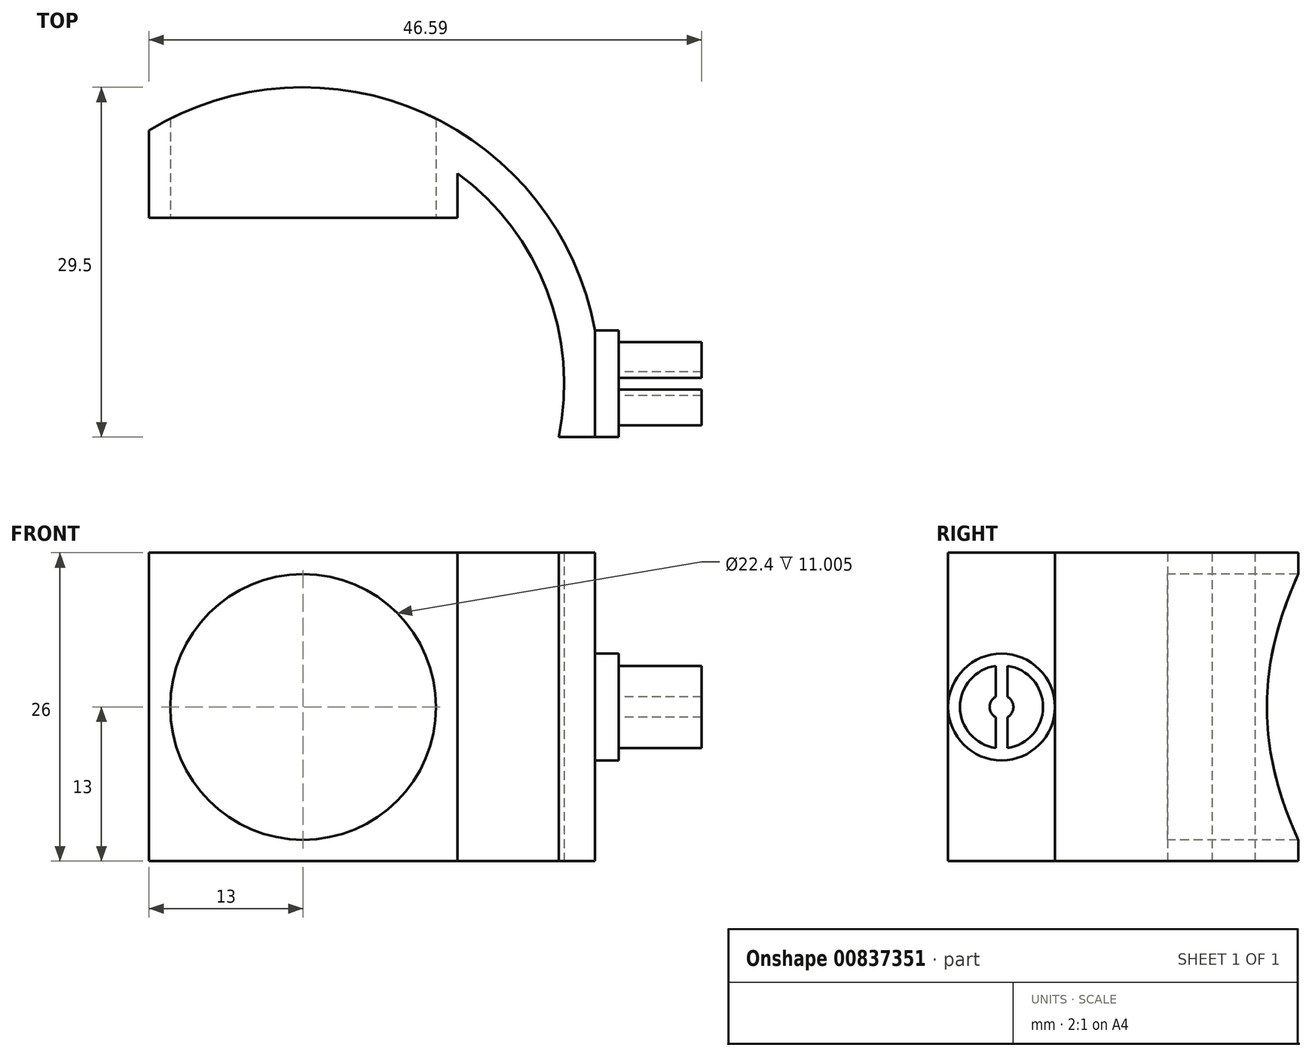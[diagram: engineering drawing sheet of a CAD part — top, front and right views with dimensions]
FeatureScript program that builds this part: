
annotation { "Feature Type Name" : "Feature", "Feature Type Description" : "" }
export const myFeature = defineFeature(function(context is Context, id is Id, definition is map)
    precondition{}
    {
        {
            var Q0;
            Q0=qCreatedBy(makeId("Top.planeOp"),FACE);
            var sketch = newSketch(context, id + "F0", { "sketchPlane" : qUnion([Q0])});
            skArc(sketch, "E0", {"start": v(21.53, -4.5) * mm, "mid": v(20.54, 7.88) * mm, "end": v(13, 17.75) * mm});
            skArc(sketch, "E1", {"start": v(24.6, 4.5) * mm, "mid": v(10.23, 22.81) * mm, "end": v(-13, 21.35) * mm});
            skLineSegment(sketch, "E2.bottom", {"start": v(13, 14) * mm, "end": v(-13, 14) * mm});
            skLineSegment(sketch, "E2.left", {"start": v(13, 14) * mm, "end": v(13, 17.75) * mm});
            skLineSegment(sketch, "E2.right", {"start": v(-13, 14) * mm, "end": v(-13, 21.35) * mm});
            skPoint(sketch, "E2.middle", {"position": v(0, 22) * mm});
            skPoint(sketch, "E2.top.end.orphan", {"position": v(-13, 30) * mm});
            skPoint(sketch, "E3.orphan", {"position": v(13, 30) * mm});
            skLineSegment(sketch, "E4", {"start": v(24.6, 4.5) * mm, "end": v(24.6, -4.5) * mm});
            skLineSegment(sketch, "E5", {"start": v(0, 0) * mm, "end": v(24.6, 0) * mm, "construction": true});
            skLineSegment(sketch, "E6", {"start": v(24.6, -4.5) * mm, "end": v(21.53, -4.5) * mm});
            skSolve(sketch);
        }
        {
            var Q0;
            Q0=makeQuery(id+"F0.imprint","IMPRINT",FACE,{"disambiguationData":[TD([[makeQuery(id+"F0.imprint","IMPRINT",EDGE,{"derivedFrom":sQuery(id+"F0.wireOp",EDGE,"E0")}),-1.0]])]});
            extrude(context, id + "F1", {"entities" : qUnion([Q0]), "depth" : 26 * mm, "offsetDistance" : 25 * mm});
        }
        {
            var Q0;
            Q0=makeQuery(id+"F1.opExtrude","SWEPT_FACE",FACE,{"disambiguationData":[OSD([sQuery(id+"F0.wireOp",EDGE,"E2.bottom")])]});
            var sketch = newSketch(context, id + "F2", { "sketchPlane" : qUnion([Q0])});
            skLineSegment(sketch, "E7", {"start": v(-13, 26) * mm, "end": v(13, 0) * mm, "construction": true});
            skLineSegment(sketch, "E8", {"start": v(-13, 0) * mm, "end": v(13, 26) * mm, "construction": true});
            skCircle(sketch, "E9", {"center": v(0, 13) * mm, "radius": 11.2 * mm});
            skSolve(sketch);
        }
        {
            var Q0;
            Q0=makeQuery(id+"F2.imprint","IMPRINT",FACE,{"disambiguationData":[TD([[makeQuery(id+"F2.imprint","IMPRINT",EDGE,{"derivedFrom":sQuery(id+"F2.wireOp",EDGE,"E9")}),1.0]])]});
            extrude(context, id + "F3", {"entities" : qUnion([Q0]), "operationType" : NewBodyOperationType.REMOVE, "oppositeDirection" : true, "depth" : 25 * mm, "offsetDistance" : 25 * mm});
        }
        {
            var Q0;
            Q0=makeQuery(id+"F1.opExtrude","SWEPT_FACE",FACE,{"disambiguationData":[OSD([sQuery(id+"F0.wireOp",EDGE,"E4")])]});
            var sketch = newSketch(context, id + "F4", { "sketchPlane" : qUnion([Q0])});
            skLineSegment(sketch, "E10", {"start": v(-4.5, 26) * mm, "end": v(4.5, 0) * mm, "construction": true});
            skLineSegment(sketch, "E11", {"start": v(-4.5, 0) * mm, "end": v(4.5, 26) * mm, "construction": true});
            skCircle(sketch, "E12", {"center": v(0, 13) * mm, "radius": 4.5 * mm});
            skSolve(sketch);
        }
        {
            var Q0;
            {var subQ0=sQuery(id+"F4.wireOp",EDGE,"E12");var subQ1=sQuery(id+"F0.wireOp",EDGE,"E4");var subQ2=makeQuery(id+"F4.imprint","INTERSECT",VERTEX,{"derivedFrom":[makeQuery(id+"F1.opExtrude","SWEPT_EDGE",EDGE,{"disambiguationData":[OSD([sQuery(id+"F0.wireOp",EDGE,"E1"),subQ1])]}),subQ0]});Q0=makeQuery(id+"F4.imprint","IMPRINT",FACE,{"disambiguationData":[TD([[makeQuery(id+"F4.imprint","IMPRINT",EDGE,{"disambiguationData":[TD([[subQ2,-1.0]])],"derivedFrom":subQ0}),1.0]])]});}
            extrude(context, id + "F5", {"entities" : qUnion([Q0]), "operationType" : NewBodyOperationType.ADD, "depth" : 2 * mm, "offsetDistance" : 25 * mm});
        }
        {
            var Q0;
            Q0=makeQuery(id+"F5.opExtrude","CAP_FACE",FACE,{"disambiguationData":[OSD([sQuery(id+"F4.wireOp",EDGE,"E12")])],"isStart":false});
            var sketch = newSketch(context, id + "F6", { "sketchPlane" : qUnion([Q0])});
            skArc(sketch, "E13", {"start": v(-0.5, 16.46) * mm, "mid": v(-3.5, 13) * mm, "end": v(-0.5, 9.54) * mm});
            skArc(sketch, "E14", {"start": v(-0.5, 13.87) * mm, "mid": v(-1, 13) * mm, "end": v(-0.5, 12.13) * mm});
            skLineSegment(sketch, "E15", {"start": v(-0.5, 16.46) * mm, "end": v(-0.5, 13.87) * mm});
            skLineSegment(sketch, "E16", {"start": v(0, 13) * mm, "end": v(1.74, 13) * mm, "construction": true});
            skLineSegment(sketch, "E17", {"start": v(0, 13) * mm, "end": v(0, 11.51) * mm, "construction": true});
            skLineSegment(sketch, "E18.MirrorCS", {"start": v(-0.5, 9.54) * mm, "end": v(-0.5, 12.13) * mm});
            skLineSegment(sketch, "E19.MirrorCS", {"start": v(0.5, 16.46) * mm, "end": v(0.5, 13.87) * mm});
            skLineSegment(sketch, "E20.MirrorCS", {"start": v(0.5, 9.54) * mm, "end": v(0.5, 12.13) * mm});
            skArc(sketch, "E21.trimOffspring", {"start": v(0.5, 12.13) * mm, "mid": v(1, 13) * mm, "end": v(0.5, 13.87) * mm});
            skArc(sketch, "E22.trimOffspring", {"start": v(0.5, 9.54) * mm, "mid": v(3.5, 13) * mm, "end": v(0.5, 16.46) * mm});
            skSolve(sketch);
        }
        {
            var Q0;
            Q0=makeQuery(id+"F6.imprint","IMPRINT",FACE,{"disambiguationData":[TD([[makeQuery(id+"F6.imprint","IMPRINT",EDGE,{"derivedFrom":sQuery(id+"F6.wireOp",EDGE,"E19.MirrorCS")}),1.0]])]});
            var Q1;
            Q1=makeQuery(id+"F6.imprint","IMPRINT",FACE,{"disambiguationData":[TD([[makeQuery(id+"F6.imprint","IMPRINT",EDGE,{"derivedFrom":sQuery(id+"F6.wireOp",EDGE,"E13")}),1.0]])]});
            extrude(context, id + "F7", {"entities" : qUnion([Q0, Q1]), "operationType" : NewBodyOperationType.ADD, "depth" : 7 * mm, "offsetDistance" : 25 * mm});
        }
    });
